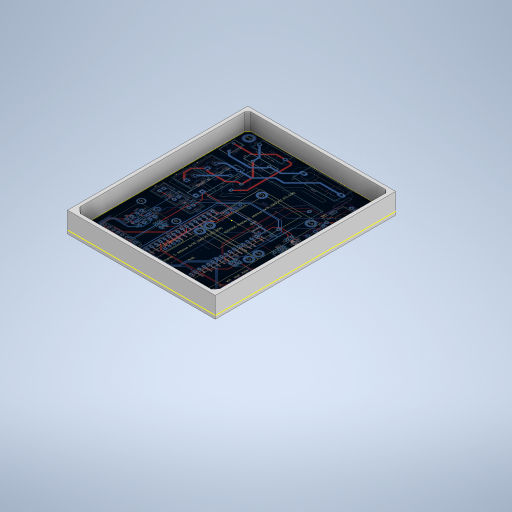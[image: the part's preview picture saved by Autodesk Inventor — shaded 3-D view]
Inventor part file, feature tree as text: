
AUTODESK INVENTOR PART (.ipt)
format: ipt  version: 2024 (Build 280153000, 153)  size: 1,205,248 bytes
history: native  units: mm
features: sketch x3, extrude x2, other x2, projected_geometry x1
ambient origin geometry x8: Origin, YZ Plane, XZ Plane, XY Plane, X Axis, Y Axis, Z Axis, Center Point
bodies: Body1 (feature_tree)
feature tree (8):
  extrude  "Extrusion3"  Depth=100.9mm
  extrude  "Extrusion4"  Depth=104.9mm
  sketch  "Sketch4"  dims[d102=10.0mm d103=0.0mm d104=2.0mm d105=0.0mm]
  sketch  "Sketch1"  dims[d48=82.0mm d49=100.9mm]
  other  "Image2"
  sketch  "Sketch3"  dims[d50=86.0mm d51=104.9mm]
  other  "Image3"
  projected_geometry  "Projected Loop1"
